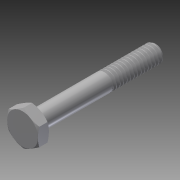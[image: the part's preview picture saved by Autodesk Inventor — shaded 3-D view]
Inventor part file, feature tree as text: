
AUTODESK INVENTOR PART (.ipt)
format: ipt  version: 2014 SP1 (Build 180222100, 222)  size: 514,560 bytes
history: native  units: in
note: dims shown in document units (in); Inventor stores cm internally (conversion verified against a paired STEP export)
features: extrude x1, other x1, imported_body x1
ambient origin geometry x8: Origin, YZ Plane, XZ Plane, XY Plane, X Axis, Y Axis, Z Axis, Center Point
bodies: Body1 (feature_tree)
feature tree (3):
  extrude  "Extrude14"  [1 undecoded]
  other  "91257A5481"
  imported_body  "Base1"
note: 1 required parameter value undecoded (feature->parameter linkage not recoverable at this tier; creation-order binding heuristic only, values carry confidence <= 0.55)
